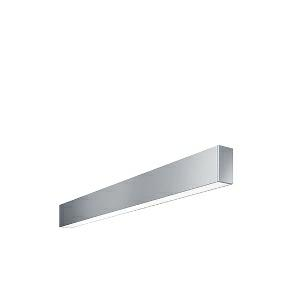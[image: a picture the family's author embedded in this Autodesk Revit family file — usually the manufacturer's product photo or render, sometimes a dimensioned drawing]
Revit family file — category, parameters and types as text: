
# Revit family: idoo_line_-_ilw_3000_830_d_00808329_8e6e
name_source: partatom
category: Lighting Fixtures
units: mm (PartAtom-declared; Revit-internal decimal feet)

## family parameters
Cut with Voids When Loaded = No
Host = Face
Light Source = No
Part Type = Normal
Room Calculation Point = No
Round Connector Dimension = Use Diameter
Shared = No

## types (1)
- IDOO.line - ILW 3000/830/D (1 x LED, 3000 lm, 3000K)
    Apparent Load = 23 VA
    Approval mark = CE
    CIE Flux Codes = 66 91 98 40 100
    Color Rendering = 80-89
    Color Temperature = 3000K
    Control Gear = Electronic ballast
    Default Elevation = 2000 mm  [stored 6.56168 ft]
    Description = ILW 3000/830/D|Wall-mounted luminaire|light source:  |work equipment: Adjustable electronic ballast, digital DALI|connected load: 220-240V, 50/60Hz|Power consumption: approx. 23 W|standby: approx. 0,25|power factor: approx. 0,970|luminous flux: 3000 lm|luminous efficacy: 130 lm/W|light distribution: Direct/indirect|direct ratio: approx. 40 %|colour temperature: Warm white, ca. 3000 K|color rendering index (CRI): >= 80|chromaticity tolerance:  3 SDCM|technology: Continuously dimmable|operation: External|luminaire body|material: Sectional aluminium|colour: Silver|lamp cover: Acrylic (PMMA), Clear|weight (net): approx. 4.7 kg|mains lead: Connector|design: Mounted version|Fastening: Mounting rail|glare control: Prism aperture|luminance(L65): <= 2700 cd/m|unified glare rating(4H 8H): <=  16|special features: DALI Load 1x, TouchDIM - dimming via standard switch, Flicker-free, Suitable as emergency lighting|
    Frequency = 50 Hz
    Height = 110 mm
    Lamp = 1 x LED
    Lamp Light Flux = 3000 lm
    Lamp count = 1
    Length = 1134 mm
    Luminous efficacy = 130 lm/W
    Manufacturer = Waldmann
    ModVariant = No
    Model = 00808329
    Mounting Place = Wall
    Mounting Type = Surface mounted
    Number of Poles = 1
    OnlyDefault = Yes
    Power Factor = 1
    Product Name = IDOO.line - ILW 3000/830/D
    Product group = Wall mounted Luminaire
    ProductGroupID = 20
    Protection Class = Protection class I
    Protection Degree = IP 40
    RLX_Detail_Level = 1
    RLX_Emergency_Light_Flux = 0 lm
    RLX_Emergency_Type = 0
    RLX_Emergency_Type_DB = No
    RlxData = <blob elided: 34497 chars, md5=21fd161d>
    Socket = socket
    Standby Power = 0 W
    System Light Flux = 3000 lm
    System Power = 23 W
    Type Comments = Product without accessories
    Type Image = 113975000-00757981.jpg
    URL = http://relux.com
    VarID = ---
    Voltage = 230 V
    Voltage Range = 220-240 V
    Weight = 0.00 kg
    Width = 60 mm  [stored 0.19685 ft]

note: [stored X ft] marks values corroborated as IEEE doubles in the binary element streams (Revit-internal decimal feet)

## geometry (parser evidence)
native form markers: Blend x4, Sweep x12
no freeform markers — native parametric forms only
